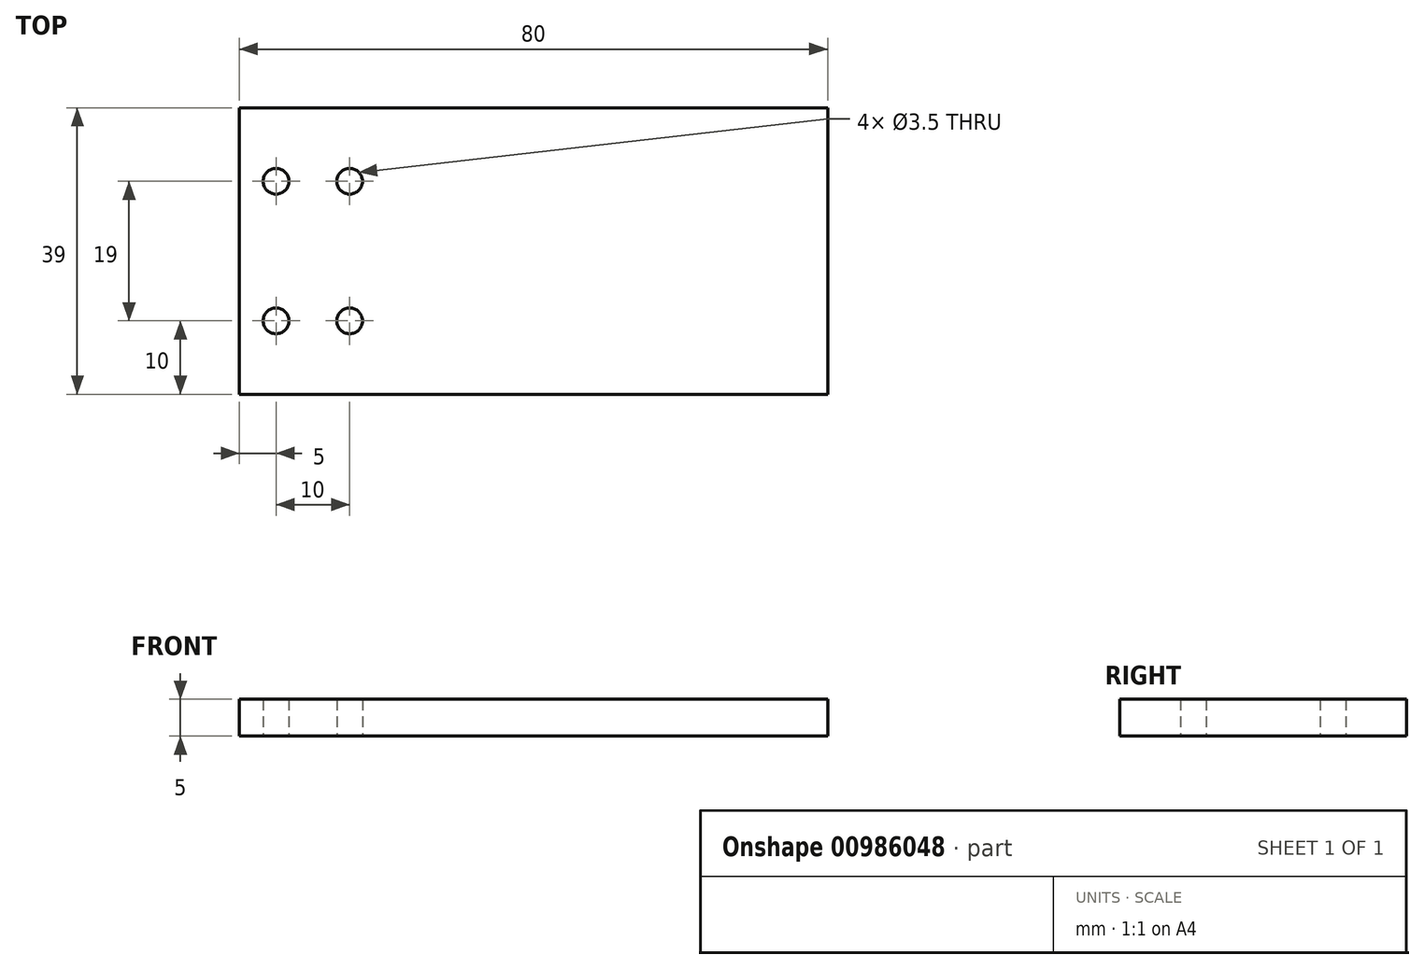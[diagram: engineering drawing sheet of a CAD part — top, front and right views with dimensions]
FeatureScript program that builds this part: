
annotation { "Feature Type Name" : "Feature", "Feature Type Description" : "" }
export const myFeature = defineFeature(function(context is Context, id is Id, definition is map)
    precondition{}
    {
        {
            var Q0;
            Q0=qCreatedBy(makeId("Top.planeOp"),FACE);
            var sketch = newSketch(context, id + "F0", { "sketchPlane" : qUnion([Q0])});
            skLineSegment(sketch, "E0.bottom", {"start": v(-40, 19.5) * mm, "end": v(40, 19.5) * mm});
            skLineSegment(sketch, "E0.top", {"start": v(-40, -19.5) * mm, "end": v(40, -19.5) * mm});
            skLineSegment(sketch, "E0.left", {"start": v(-40, 19.5) * mm, "end": v(-40, -19.5) * mm});
            skLineSegment(sketch, "E0.right", {"start": v(40, 19.5) * mm, "end": v(40, -19.5) * mm});
            skLineSegment(sketch, "E1", {"start": v(-35, 32.65) * mm, "end": v(-35, -33.8) * mm, "construction": true});
            skLineSegment(sketch, "E2", {"start": v(-25, 32.65) * mm, "end": v(-25, -33.8) * mm, "construction": true});
            skLineSegment(sketch, "E3", {"start": v(-65.07, 9.5) * mm, "end": v(16.98, 9.5) * mm, "construction": true});
            skCircle(sketch, "E4", {"center": v(-35, 9.5) * mm, "radius": 1.75 * mm});
            skCircle(sketch, "E5", {"center": v(-25, 9.5) * mm, "radius": 1.75 * mm});
            skCircle(sketch, "E6", {"center": v(-35, -9.5) * mm, "radius": 1.75 * mm});
            skCircle(sketch, "E7", {"center": v(-25, -9.5) * mm, "radius": 1.75 * mm});
            skSolve(sketch);
        }
        {
            var Q0;
            Q0=makeQuery(id+"F0.imprint","IMPRINT",FACE,{"disambiguationData":[TD([[makeQuery(id+"F0.imprint","IMPRINT",EDGE,{"derivedFrom":sQuery(id+"F0.wireOp",EDGE,"E0.bottom")}),-1.0]])]});
            extrude(context, id + "F1", {"entities" : qUnion([Q0]), "depth" : 5 * mm, "offsetDistance" : 25 * mm});
        }
    });
